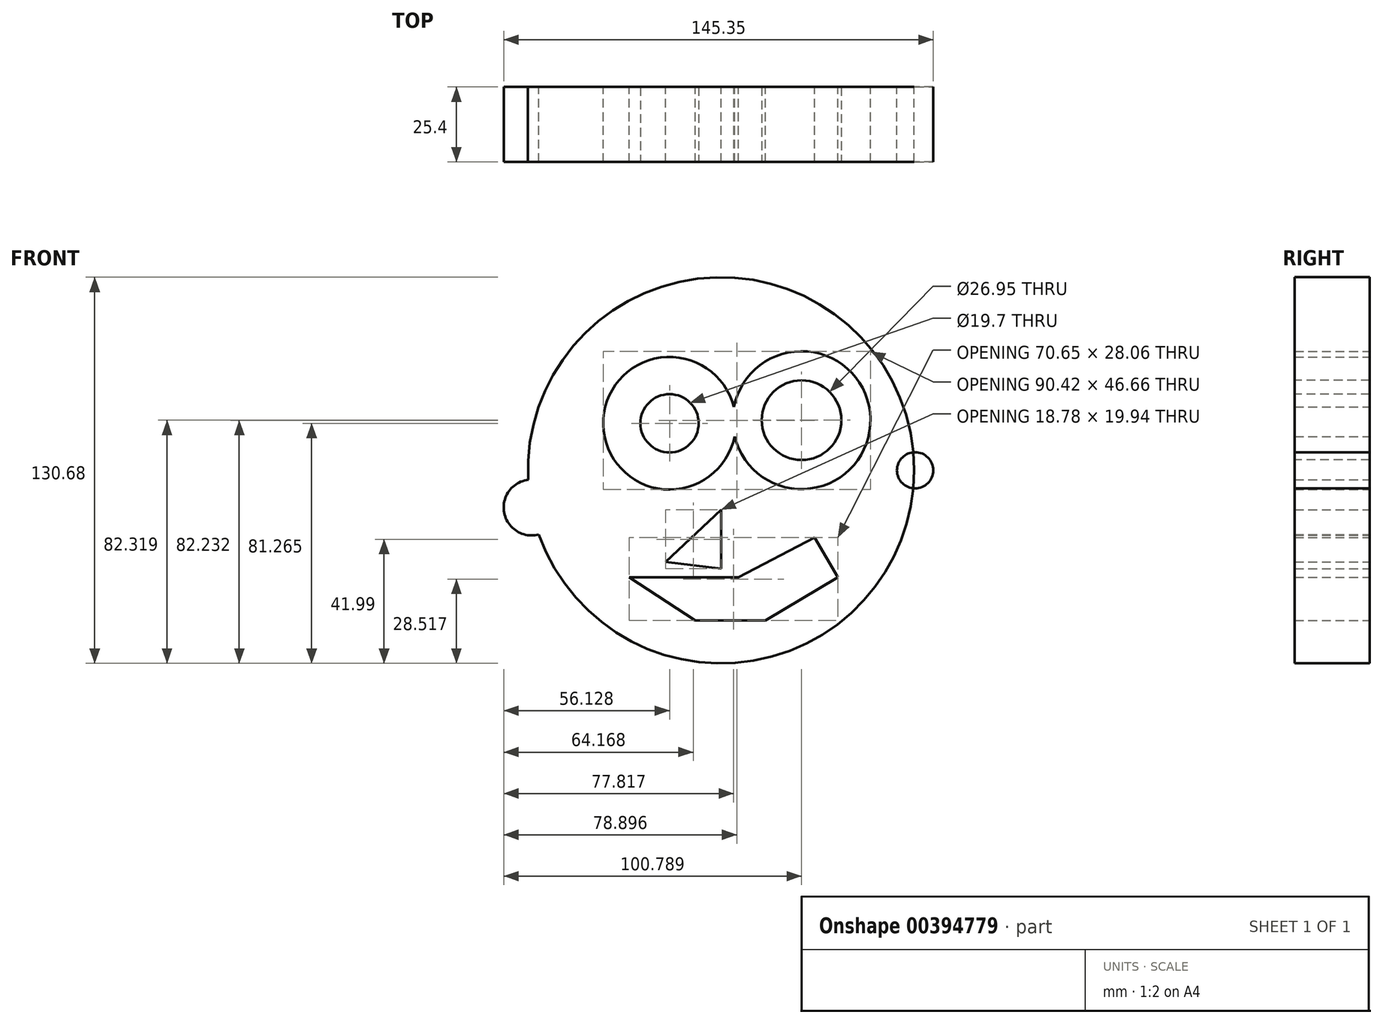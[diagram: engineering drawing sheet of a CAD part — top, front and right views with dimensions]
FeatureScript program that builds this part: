
annotation { "Feature Type Name" : "Feature", "Feature Type Description" : "" }
export const myFeature = defineFeature(function(context is Context, id is Id, definition is map)
    precondition{}
    {
        {
            var Q0;
            Q0=qCreatedBy(makeId("Front.planeOp"),FACE);
            var sketch = newSketch(context, id + "F0", { "sketchPlane" : qUnion([Q0])});
            skCircle(sketch, "E0", {"center": v(0, 0) * mm, "radius": 65.34 * mm});
            skCircle(sketch, "E1", {"center": v(-17.43, 15.92) * mm, "radius": 22.45 * mm});
            skCircle(sketch, "E2", {"center": v(27.23, 16.98) * mm, "radius": 23.32 * mm});
            skCircle(sketch, "E3", {"center": v(27.23, 16.98) * mm, "radius": 8.54 * mm});
            skCircle(sketch, "E4", {"center": v(-17.43, 15.92) * mm, "radius": 9.06 * mm});
            skLineSegment(sketch, "E5", {"start": v(0, -13.38) * mm, "end": v(-18.78, -30.99) * mm});
            skLineSegment(sketch, "E6", {"start": v(-18.78, -30.99) * mm, "end": v(0, -33.32) * mm});
            skLineSegment(sketch, "E7", {"start": v(0, -33.32) * mm, "end": v(0, -13.38) * mm});
            skCircle(sketch, "E8", {"center": v(-64.12, -12.59) * mm, "radius": 9.44 * mm});
            skSolve(sketch);
        }
        {
            var Q0;
            Q0=qCreatedBy(makeId("Front.planeOp"),FACE);
            var sketch = newSketch(context, id + "F1", { "sketchPlane" : qUnion([Q0])});
            skCircle(sketch, "E9", {"center": v(65.65, 0) * mm, "radius": 6.13 * mm});
            skSolve(sketch);
        }
        {
            var Q0;
            Q0=makeQuery(id+"F0.imprint","IMPRINT",FACE,{"disambiguationData":[TD([[makeQuery(id+"F0.imprint","IMPRINT",EDGE,{"derivedFrom":sQuery(id+"F0.wireOp",EDGE,"E5")}),-1.0]])]});
            var sketch = newSketch(context, id + "F2", { "sketchPlane" : qUnion([Q0])});
            skSolve(sketch);
        }
        {
            var Q0;
            Q0=makeQuery(id+"F0.imprint","IMPRINT",FACE,{"disambiguationData":[TD([[makeQuery(id+"F0.imprint","IMPRINT",EDGE,{"derivedFrom":sQuery(id+"F0.wireOp",EDGE,"E5")}),-1.0]])]});
            var sketch = newSketch(context, id + "F3", { "sketchPlane" : qUnion([Q0])});
            skSolve(sketch);
        }
        {
            var Q0;
            Q0=makeQuery(id+"F0.imprint","IMPRINT",FACE,{"disambiguationData":[TD([[makeQuery(id+"F0.imprint","IMPRINT",EDGE,{"derivedFrom":sQuery(id+"F0.wireOp",EDGE,"E5")}),-1.0]])]});
            var Q1;
            Q1=makeQuery(id+"F1.imprint","IMPRINT",FACE,{"disambiguationData":[TD([[makeQuery(id+"F1.imprint","IMPRINT",EDGE,{"derivedFrom":sQuery(id+"F1.wireOp",EDGE,"E9")}),1.0]])]});
            var Q2;
            {var subQ0=sQuery(id+"F0.wireOp",EDGE,"E2");var subQ1=sQuery(id+"F0.wireOp",EDGE,"E1");var subQ2=makeQuery(id+"F0.imprint","INTERSECT",VERTEX,{"disambiguationData":[OD(0.0)],"derivedFrom":[subQ1,subQ0]});Q2=makeQuery(id+"F2.imprint","IMPRINT",FACE,{"disambiguationData":[TD([[makeQuery(id+"F2.imprint","IMPRINT",EDGE,{"derivedFrom":makeQuery(id+"F0.imprint","IMPRINT",EDGE,{"disambiguationData":[TD([[subQ2,1.0]])],"derivedFrom":subQ1})}),1.0]])]});}
            var Q3;
            {var subQ0=sQuery(id+"F0.wireOp",EDGE,"E8");var subQ1=sQuery(id+"F0.wireOp",EDGE,"E0");var subQ2=makeQuery(id+"F0.imprint","INTERSECT",VERTEX,{"disambiguationData":[OD(0.0)],"derivedFrom":[subQ1,subQ0]});Q3=makeQuery(id+"F0.imprint","IMPRINT",FACE,{"disambiguationData":[TD([[makeQuery(id+"F0.imprint","IMPRINT",EDGE,{"disambiguationData":[TD([[subQ2,1.0]])],"derivedFrom":subQ1}),-1.0]])]});}
            var Q4;
            {var subQ0=sQuery(id+"F0.wireOp",EDGE,"E8");var subQ1=sQuery(id+"F0.wireOp",EDGE,"E0");var subQ2=makeQuery(id+"F0.imprint","INTERSECT",VERTEX,{"disambiguationData":[OD(0.0)],"derivedFrom":[subQ1,subQ0]});Q4=makeQuery(id+"F0.imprint","IMPRINT",FACE,{"disambiguationData":[TD([[makeQuery(id+"F0.imprint","IMPRINT",EDGE,{"disambiguationData":[TD([[subQ2,1.0]])],"derivedFrom":subQ1}),1.0]])]});}
            var Q5;
            Q5=makeQuery(id+"F0.imprint","IMPRINT",FACE,{"disambiguationData":[TD([[makeQuery(id+"F0.imprint","IMPRINT",EDGE,{"derivedFrom":sQuery(id+"F0.wireOp",EDGE,"E5")}),1.0]])]});
            extrude(context, id + "F4", {"entities" : qUnion([Q0, Q1, Q2, Q3, Q4, Q5]), "depth" : 25.4 * mm});
        }
        {
            var Q0;
            Q0=makeQuery(id+"F4.opExtrude","CAP_FACE",FACE,{"disambiguationData":[OSD([sQuery(id+"F0.wireOp",EDGE,"E1"),sQuery(id+"F0.wireOp",EDGE,"E2")])],"isStart":false});
            var sketch = newSketch(context, id + "F5", { "sketchPlane" : qUnion([Q0])});
            skCircle(sketch, "E10", {"center": v(-17.43, 15.92) * mm, "radius": 9.85 * mm});
            skCircle(sketch, "E11", {"center": v(27.23, 16.98) * mm, "radius": 13.48 * mm});
            skSolve(sketch);
        }
        {
            var Q0;
            Q0 = qSketchRegion(id + "F5", true);
            extrude(context, id + "F6", {"entities" : qUnion([Q0]), "operationType" : NewBodyOperationType.REMOVE, "oppositeDirection" : true, "depth" : 50.8 * mm});
        }
        {
            var Q0;
            Q0=makeQuery(id+"F3.imprint","IMPRINT",FACE,{"disambiguationData":[TD([[makeQuery(id+"F3.imprint","IMPRINT",EDGE,{"derivedFrom":makeQuery(id+"F0.imprint","IMPRINT",EDGE,{"derivedFrom":sQuery(id+"F0.wireOp",EDGE,"E5")})}),-1.0]])]});
            var sketch = newSketch(context, id + "F7", { "sketchPlane" : qUnion([Q0])});
            skSolve(sketch);
        }
        {
            var Q0;
            Q0=makeQuery(id+"F3.imprint","IMPRINT",FACE,{"disambiguationData":[TD([[makeQuery(id+"F3.imprint","IMPRINT",EDGE,{"derivedFrom":makeQuery(id+"F0.imprint","IMPRINT",EDGE,{"derivedFrom":sQuery(id+"F0.wireOp",EDGE,"E5")})}),1.0]])]});
            extrude(context, id + "F8", {"entities" : qUnion([Q0]), "operationType" : NewBodyOperationType.REMOVE, "depth" : 50.8 * mm});
        }
        {
            var Q0;
            Q0=makeQuery(id+"F7.imprint","IMPRINT",FACE,{"disambiguationData":[TD([[makeQuery(id+"F7.imprint","IMPRINT",EDGE,{"derivedFrom":makeQuery(id+"F3.imprint","IMPRINT",EDGE,{"derivedFrom":makeQuery(id+"F0.imprint","IMPRINT",EDGE,{"derivedFrom":sQuery(id+"F0.wireOp",EDGE,"E5")})})}),-1.0]])]});
            var sketch = newSketch(context, id + "F9", { "sketchPlane" : qUnion([Q0])});
            skLineSegment(sketch, "E12", {"start": v(31.6, -22.8) * mm, "end": v(39.58, -36.17) * mm});
            skLineSegment(sketch, "E13", {"start": v(39.58, -36.17) * mm, "end": v(14.96, -50.85) * mm});
            skLineSegment(sketch, "E14", {"start": v(14.96, -50.85) * mm, "end": v(-8.71, -50.85) * mm});
            skLineSegment(sketch, "E15", {"start": v(-8.71, -50.85) * mm, "end": v(-31.07, -36.17) * mm});
            skLineSegment(sketch, "E16", {"start": v(-31.07, -36.17) * mm, "end": v(-18.26, -36.17) * mm});
            skLineSegment(sketch, "E17", {"start": v(-18.26, -36.17) * mm, "end": v(5.89, -36.17) * mm});
            skLineSegment(sketch, "E18", {"start": v(5.89, -36.17) * mm, "end": v(31.6, -22.8) * mm});
            skSolve(sketch);
        }
        {
            var Q0;
            Q0=makeQuery(id+"F9.imprint","IMPRINT",FACE,{"disambiguationData":[TD([[makeQuery(id+"F9.imprint","IMPRINT",EDGE,{"derivedFrom":sQuery(id+"F9.wireOp",EDGE,"E12")}),-1.0]])]});
            extrude(context, id + "F10", {"entities" : qUnion([Q0]), "operationType" : NewBodyOperationType.REMOVE, "depth" : 25.4 * mm});
        }
    });
